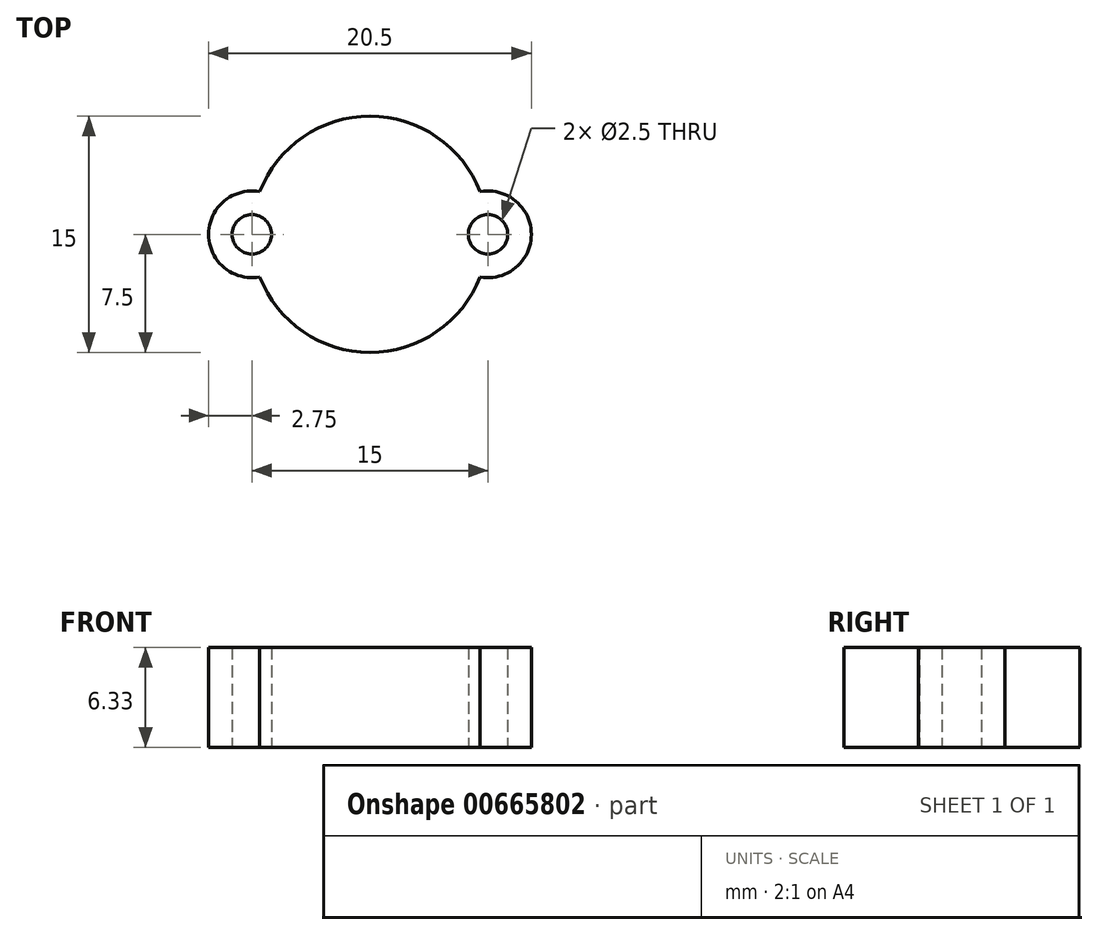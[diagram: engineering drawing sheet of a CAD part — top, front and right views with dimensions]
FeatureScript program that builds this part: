
annotation { "Feature Type Name" : "Feature", "Feature Type Description" : "" }
export const myFeature = defineFeature(function(context is Context, id is Id, definition is map)
    precondition{}
    {
        {
            var Q0;
            Q0=qCreatedBy(makeId("Top.planeOp"),FACE);
            var sketch = newSketch(context, id + "F0", { "sketchPlane" : qUnion([Q0])});
            skArc(sketch, "E0", {"start": v(7, 2.7) * mm, "mid": v(0, 7.5) * mm, "end": v(-7, 2.7) * mm});
            skCircle(sketch, "E1", {"center": v(-7.5, 0) * mm, "radius": 1.25 * mm});
            skCircle(sketch, "E2.MirrorC", {"center": v(7.5, 0) * mm, "radius": 1.25 * mm});
            skArc(sketch, "E3", {"start": v(-7, 2.7) * mm, "mid": v(-10.25, 0) * mm, "end": v(-7, -2.7) * mm});
            skArc(sketch, "E4.MirrorC", {"start": v(7, 2.7) * mm, "mid": v(10.25, 0) * mm, "end": v(7, -2.7) * mm});
            skArc(sketch, "E5.trimOffspring", {"start": v(-7, -2.7) * mm, "mid": v(0, -7.5) * mm, "end": v(7, -2.7) * mm});
            skSolve(sketch);
        }
        {
            var Q0;
            Q0 = qSketchRegion(id + "F0", true);
            extrude(context, id + "F1", {"entities" : qUnion([Q0]), "depth" : 9.5 * mm * 2 / 3, "offsetDistance" : 25.4 * mm});
        }
    });
